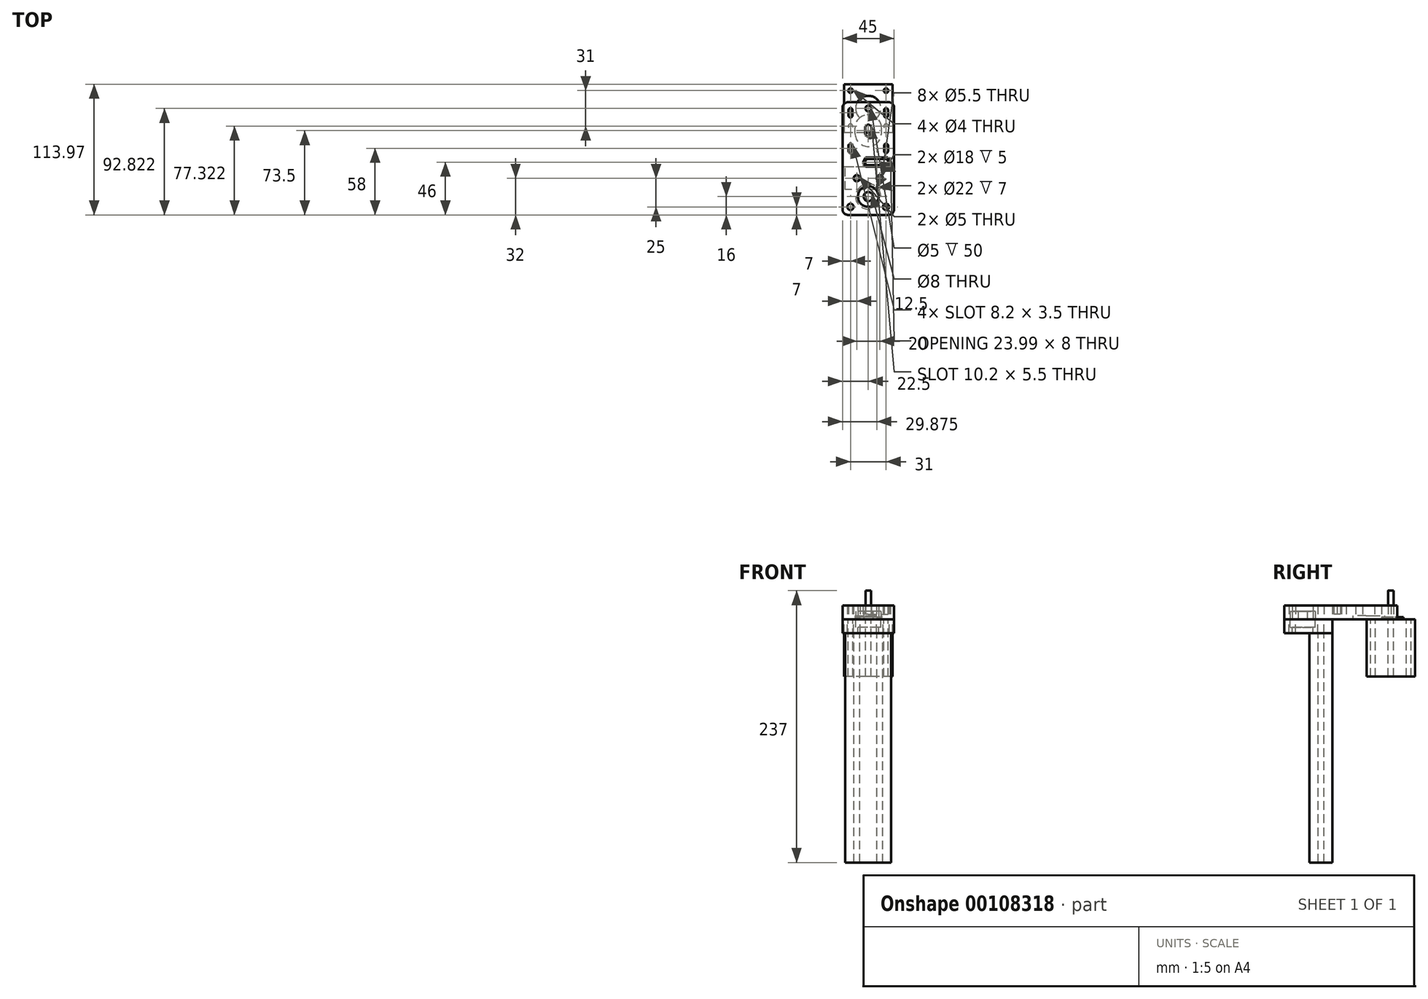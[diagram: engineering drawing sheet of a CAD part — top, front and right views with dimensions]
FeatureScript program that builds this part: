
annotation { "Feature Type Name" : "Feature", "Feature Type Description" : "" }
export const myFeature = defineFeature(function(context is Context, id is Id, definition is map)
    precondition{}
    {
        {
            var Q0;
            Q0=qCreatedBy(makeId("Top.planeOp"),FACE);
            var sketch = newSketch(context, id + "F0", { "sketchPlane" : qUnion([Q0])});
            skCircle(sketch, "E0", {"center": v(0, 76.82) * mm, "radius": 11 * mm});
            skLineSegment(sketch, "E1.bottom", {"start": v(21.15, 97.97) * mm, "end": v(-21.15, 97.97) * mm});
            skLineSegment(sketch, "E1.top", {"start": v(21.15, 55.67) * mm, "end": v(-21.15, 55.67) * mm});
            skLineSegment(sketch, "E1.left", {"start": v(21.15, 97.97) * mm, "end": v(21.15, 55.67) * mm});
            skLineSegment(sketch, "E1.right", {"start": v(-21.15, 97.97) * mm, "end": v(-21.15, 55.67) * mm});
            skLineSegment(sketch, "E2.bottom", {"start": v(15.5, 92.32) * mm, "end": v(-15.5, 92.32) * mm, "construction": true});
            skLineSegment(sketch, "E2.top", {"start": v(15.5, 61.32) * mm, "end": v(-15.5, 61.32) * mm, "construction": true});
            skLineSegment(sketch, "E2.left", {"start": v(15.5, 92.32) * mm, "end": v(15.5, 61.32) * mm, "construction": true});
            skLineSegment(sketch, "E2.right", {"start": v(-15.5, 92.32) * mm, "end": v(-15.5, 61.32) * mm, "construction": true});
            skCircle(sketch, "E3", {"center": v(-15.5, 92.32) * mm, "radius": 2 * mm});
            skCircle(sketch, "E4", {"center": v(15.5, 92.32) * mm, "radius": 2 * mm});
            skCircle(sketch, "E5", {"center": v(15.5, 61.32) * mm, "radius": 2 * mm});
            skCircle(sketch, "E6", {"center": v(-15.5, 61.32) * mm, "radius": 2 * mm});
            skCircle(sketch, "E7", {"center": v(0, 76.82) * mm, "radius": 2.5 * mm});
            skSolve(sketch);
        }
        {
            var Q0;
            Q0=qCreatedBy(makeId("Top.planeOp"),FACE);
            var sketch = newSketch(context, id + "F1", { "sketchPlane" : qUnion([Q0])});
            skCircle(sketch, "E8", {"center": v(0, 0) * mm, "radius": 4 * mm});
            skCircle(sketch, "E9", {"center": v(0, 0) * mm, "radius": 11 * mm});
            skSolve(sketch);
        }
        {
            var Q0;
            Q0=makeQuery(id+"F1.imprint","IMPRINT",FACE,{"disambiguationData":[TD([[makeQuery(id+"F1.imprint","IMPRINT",EDGE,{"derivedFrom":sQuery(id+"F1.wireOp",EDGE,"E8")}),-1.0]])]});
            extrude(context, id + "F2", {"entities" : qUnion([Q0]), "depth" : 7 * mm});
        }
        {
            var Q0;
            Q0=makeQuery(id+"F0.imprint","IMPRINT",FACE,{"disambiguationData":[TD([[makeQuery(id+"F0.imprint","IMPRINT",EDGE,{"derivedFrom":sQuery(id+"F0.wireOp",EDGE,"E0")}),-1.0]])]});
            var Q1;
            Q1=makeQuery(id+"F0.imprint","IMPRINT",FACE,{"disambiguationData":[TD([[makeQuery(id+"F0.imprint","IMPRINT",EDGE,{"derivedFrom":sQuery(id+"F0.wireOp",EDGE,"E0")}),1.0]])]});
            extrude(context, id + "F3", {"entities" : qUnion([Q0, Q1]), "oppositeDirection" : true, "depth" : 50 * mm});
        }
        {
            var Q0;
            Q0=makeQuery(id+"F0.imprint","IMPRINT",FACE,{"disambiguationData":[TD([[makeQuery(id+"F0.imprint","IMPRINT",EDGE,{"derivedFrom":sQuery(id+"F0.wireOp",EDGE,"E0")}),1.0]])]});
            extrude(context, id + "F4", {"entities" : qUnion([Q0]), "operationType" : NewBodyOperationType.ADD, "depth" : 2 * mm});
        }
        {
            var Q0;
            Q0=makeQuery(id+"F0.imprint","IMPRINT",FACE,{"disambiguationData":[TD([[makeQuery(id+"F0.imprint","IMPRINT",EDGE,{"derivedFrom":sQuery(id+"F0.wireOp",EDGE,"E7")}),1.0]])]});
            extrude(context, id + "F5", {"entities" : qUnion([Q0]), "operationType" : NewBodyOperationType.ADD, "depth" : 25 * mm});
        }
        {
            var Q0;
            Q0=qCreatedBy(makeId("Top.planeOp"),FACE);
            var sketch = newSketch(context, id + "F6", { "sketchPlane" : qUnion([Q0])});
            skCircle(sketch, "E10", {"center": v(0, 0) * mm, "radius": 11 * mm});
            skCircle(sketch, "E11", {"center": v(0, 0) * mm, "radius": 9 * mm});
            skLineSegment(sketch, "E12", {"start": v(0, -16) * mm, "end": v(17.5, -16) * mm});
            skLineSegment(sketch, "E13", {"start": v(22.5, -11) * mm, "end": v(22.5, 77.35) * mm});
            skLineSegment(sketch, "E14", {"start": v(17.5, 82.35) * mm, "end": v(-17.5, 82.35) * mm});
            skLineSegment(sketch, "E15", {"start": v(-22.5, 77.35) * mm, "end": v(-22.5, -11) * mm});
            skLineSegment(sketch, "E16", {"start": v(-17.5, -16) * mm, "end": v(0, -16) * mm});
            skLineSegment(sketch, "E17", {"start": v(0, 0) * mm, "end": v(22.5, 0) * mm, "construction": true});
            skCircle(sketch, "E18", {"center": v(-10, 16) * mm, "radius": 2.75 * mm});
            skCircle(sketch, "E19", {"center": v(10, 16) * mm, "radius": 2.75 * mm});
            skLineSegment(sketch, "E20", {"start": v(-10, 16) * mm, "end": v(0, 16) * mm, "construction": true});
            skLineSegment(sketch, "E21", {"start": v(0, 16) * mm, "end": v(10, 16) * mm, "construction": true});
            skArc(sketch, "E22", {"start": v(-11.5, 55.15) * mm, "mid": v(0, 43.65) * mm, "end": v(11.5, 55.15) * mm});
            skLineSegment(sketch, "E23", {"start": v(-11.5, 55.15) * mm, "end": v(-11.5, 59.85) * mm});
            skLineSegment(sketch, "E24", {"start": v(11.5, 55.15) * mm, "end": v(11.5, 59.85) * mm});
            skArc(sketch, "E25", {"start": v(-11.5, 59.85) * mm, "mid": v(0, 71.35) * mm, "end": v(11.5, 59.85) * mm});
            skLineSegment(sketch, "E26.bottom", {"start": v(15.5, 75.35) * mm, "end": v(-15.5, 75.35) * mm, "construction": true});
            skLineSegment(sketch, "E26.top", {"start": v(15.5, 44.35) * mm, "end": v(-15.5, 44.35) * mm, "construction": true});
            skLineSegment(sketch, "E26.left", {"start": v(15.5, 75.35) * mm, "end": v(15.5, 44.35) * mm, "construction": true});
            skLineSegment(sketch, "E26.right", {"start": v(-15.5, 75.35) * mm, "end": v(-15.5, 44.35) * mm, "construction": true});
            skLineSegment(sketch, "E27.bottom", {"start": v(15.5, 70.65) * mm, "end": v(-15.5, 70.65) * mm, "construction": true});
            skLineSegment(sketch, "E27.top", {"start": v(15.5, 39.65) * mm, "end": v(-15.5, 39.65) * mm, "construction": true});
            skLineSegment(sketch, "E27.left", {"start": v(15.5, 70.65) * mm, "end": v(15.5, 39.65) * mm, "construction": true});
            skLineSegment(sketch, "E27.right", {"start": v(-15.5, 70.65) * mm, "end": v(-15.5, 39.65) * mm, "construction": true});
            skArc(sketch, "E28", {"start": v(-17.25, 75.35) * mm, "mid": v(-15.5, 77.1) * mm, "end": v(-13.75, 75.35) * mm});
            skArc(sketch, "E29", {"start": v(13.75, 75.35) * mm, "mid": v(15.5, 77.1) * mm, "end": v(17.25, 75.35) * mm});
            skArc(sketch, "E30", {"start": v(-17.25, 70.65) * mm, "mid": v(-15.5, 68.9) * mm, "end": v(-13.75, 70.65) * mm});
            skArc(sketch, "E31", {"start": v(13.75, 70.65) * mm, "mid": v(15.5, 68.9) * mm, "end": v(17.25, 70.65) * mm});
            skLineSegment(sketch, "E32", {"start": v(-17.25, 70.65) * mm, "end": v(-17.25, 75.35) * mm});
            skLineSegment(sketch, "E33", {"start": v(-13.75, 70.65) * mm, "end": v(-13.75, 75.35) * mm});
            skLineSegment(sketch, "E34", {"start": v(13.75, 70.65) * mm, "end": v(13.75, 75.35) * mm});
            skLineSegment(sketch, "E35", {"start": v(17.25, 70.65) * mm, "end": v(17.25, 75.35) * mm});
            skArc(sketch, "E36", {"start": v(-17.25, 44.35) * mm, "mid": v(-15.5, 46.1) * mm, "end": v(-13.75, 44.35) * mm});
            skArc(sketch, "E37", {"start": v(13.75, 44.35) * mm, "mid": v(15.5, 46.1) * mm, "end": v(17.25, 44.35) * mm});
            skArc(sketch, "E38", {"start": v(-17.25, 39.65) * mm, "mid": v(-15.5, 37.9) * mm, "end": v(-13.75, 39.65) * mm});
            skArc(sketch, "E39", {"start": v(13.75, 39.65) * mm, "mid": v(15.5, 37.9) * mm, "end": v(17.25, 39.65) * mm});
            skLineSegment(sketch, "E40", {"start": v(-17.25, 39.65) * mm, "end": v(-17.25, 44.35) * mm});
            skLineSegment(sketch, "E41", {"start": v(-13.75, 39.65) * mm, "end": v(-13.75, 44.35) * mm});
            skLineSegment(sketch, "E42", {"start": v(13.75, 39.65) * mm, "end": v(13.75, 44.35) * mm});
            skLineSegment(sketch, "E43", {"start": v(17.25, 39.65) * mm, "end": v(17.25, 44.35) * mm});
            skArc(sketch, "E44", {"start": v(-2.75, 59.85) * mm, "mid": v(0, 62.6) * mm, "end": v(2.75, 59.85) * mm});
            skArc(sketch, "E45", {"start": v(-2.75, 55.15) * mm, "mid": v(0, 52.4) * mm, "end": v(2.75, 55.15) * mm});
            skLineSegment(sketch, "E46", {"start": v(-2.75, 55.15) * mm, "end": v(-2.75, 59.85) * mm});
            skLineSegment(sketch, "E47", {"start": v(2.75, 59.85) * mm, "end": v(2.75, 55.15) * mm});
            skLineSegment(sketch, "E48", {"start": v(0, 59.85) * mm, "end": v(22.5, 59.85) * mm, "construction": true});
            skLineSegment(sketch, "E49", {"start": v(0, 59.85) * mm, "end": v(0, 82.35) * mm, "construction": true});
            skPoint(sketch, "E50.visualSharp", {"position": v(-22.5, 82.35) * mm});
            skArc(sketch, "E50.filletArc", {"start": v(-17.5, 82.35) * mm, "mid": v(-21.04, 80.89) * mm, "end": v(-22.5, 77.35) * mm});
            skPoint(sketch, "E51.visualSharp", {"position": v(22.5, 82.35) * mm});
            skArc(sketch, "E51.filletArc", {"start": v(22.5, 77.35) * mm, "mid": v(21.04, 80.89) * mm, "end": v(17.5, 82.35) * mm});
            skPoint(sketch, "E52.visualSharp", {"position": v(22.5, -16) * mm});
            skArc(sketch, "E52.filletArc", {"start": v(17.5, -16) * mm, "mid": v(21.04, -14.54) * mm, "end": v(22.5, -11) * mm});
            skPoint(sketch, "E53.visualSharp", {"position": v(-22.5, -16) * mm});
            skArc(sketch, "E53.filletArc", {"start": v(-22.5, -11) * mm, "mid": v(-21.04, -14.54) * mm, "end": v(-17.5, -16) * mm});
            skLineSegment(sketch, "E54.bottom", {"start": v(20, 26) * mm, "end": v(-20, 26) * mm, "construction": true});
            skLineSegment(sketch, "E54.top", {"start": v(20, 6) * mm, "end": v(-20, 6) * mm, "construction": true});
            skLineSegment(sketch, "E54.left", {"start": v(20, 26) * mm, "end": v(20, 6) * mm, "construction": true});
            skLineSegment(sketch, "E54.right", {"start": v(-20, 26) * mm, "end": v(-20, 6) * mm, "construction": true});
            skPoint(sketch, "E54.middle", {"position": v(0, 16) * mm});
            skCircle(sketch, "E55", {"center": v(0, 0) * mm, "radius": 4 * mm});
            skLineSegment(sketch, "E56", {"start": v(-21.15, 34) * mm, "end": v(21.15, 34) * mm, "construction": true});
            skLineSegment(sketch, "E57", {"start": v(21.15, 34) * mm, "end": v(21.15, 81) * mm, "construction": true});
            skLineSegment(sketch, "E58", {"start": v(21.15, 81) * mm, "end": v(-21.15, 81) * mm, "construction": true});
            skLineSegment(sketch, "E59", {"start": v(-21.15, 81) * mm, "end": v(-21.15, 34) * mm, "construction": true});
            skPoint(sketch, "E60", {"position": v(0, 34) * mm});
            skLineSegment(sketch, "E61", {"start": v(15.5, 39.65) * mm, "end": v(21.15, 39.65) * mm, "construction": true});
            skLineSegment(sketch, "E62", {"start": v(15.5, 39.65) * mm, "end": v(15.5, 34) * mm, "construction": true});
            skLineSegment(sketch, "E63", {"start": v(15.5, 75.35) * mm, "end": v(15.5, 81) * mm, "construction": true});
            skLineSegment(sketch, "E64", {"start": v(-22.5, 26) * mm, "end": v(22.5, 26) * mm});
            skCircle(sketch, "E65", {"center": v(15.5, -9) * mm, "radius": 2.75 * mm});
            skCircle(sketch, "E66", {"center": v(-15.5, -9) * mm, "radius": 2.75 * mm});
            skLineSegment(sketch, "E67", {"start": v(22.5, -9) * mm, "end": v(15.5, -9) * mm, "construction": true});
            skLineSegment(sketch, "E68", {"start": v(-15.5, -9) * mm, "end": v(-22.5, -9) * mm, "construction": true});
            skCircle(sketch, "E69", {"center": v(0, 0) * mm, "radius": 10.2 * mm, "construction": true});
            skArc(sketch, "E70", {"start": v(0, 27.25) * mm, "mid": v(-2.75, 30) * mm, "end": v(0, 32.75) * mm});
            skArc(sketch, "E71", {"start": v(14.75, 32.75) * mm, "mid": v(17.5, 30) * mm, "end": v(14.75, 27.25) * mm});
            skLineSegment(sketch, "E72", {"start": v(0, 32.75) * mm, "end": v(14.75, 32.75) * mm});
            skLineSegment(sketch, "E73", {"start": v(14.75, 27.25) * mm, "end": v(0, 27.25) * mm});
            skLineSegment(sketch, "E74", {"start": v(0, 34) * mm, "end": v(0, 26) * mm, "construction": true});
            skCircle(sketch, "E75", {"center": v(0, 0) * mm, "radius": 12.75 * mm, "construction": true});
            skCircle(sketch, "E76", {"center": v(0, 55.15) * mm, "radius": 12.75 * mm, "construction": true});
            skLineSegment(sketch, "E77", {"start": v(12.75, 55.15) * mm, "end": v(12.75, 0) * mm, "construction": true});
            skLineSegment(sketch, "E78", {"start": v(-12.75, 55.15) * mm, "end": v(-12.75, 0) * mm, "construction": true});
            skCircle(sketch, "E79", {"center": v(0, 30) * mm, "radius": 6.35 * mm, "construction": true});
            skCircle(sketch, "E80", {"center": v(14.75, 30) * mm, "radius": 6.35 * mm, "construction": true});
            skLineSegment(sketch, "E81", {"start": v(15.5, -9) * mm, "end": v(15.5, -16) * mm, "construction": true});
            skLineSegment(sketch, "E82", {"start": v(-4.62, 30) * mm, "end": v(-2.3, 26) * mm});
            skLineSegment(sketch, "E83", {"start": v(-4.62, 30) * mm, "end": v(-2.3, 34) * mm});
            skLineSegment(sketch, "E84", {"start": v(-2.3, 34) * mm, "end": v(17.06, 34) * mm});
            skLineSegment(sketch, "E85", {"start": v(17.06, 34) * mm, "end": v(19.37, 30) * mm});
            skLineSegment(sketch, "E86", {"start": v(19.37, 30) * mm, "end": v(17.06, 26) * mm});
            skLineSegment(sketch, "E87", {"start": v(18.21, 28) * mm, "end": v(14.75, 30) * mm, "construction": true});
            skLineSegment(sketch, "E88", {"start": v(18.21, 32) * mm, "end": v(14.75, 30) * mm, "construction": true});
            skLineSegment(sketch, "E89", {"start": v(-3.46, 32) * mm, "end": v(0, 30) * mm, "construction": true});
            skLineSegment(sketch, "E90", {"start": v(-3.46, 28) * mm, "end": v(0, 30) * mm, "construction": true});
            skPoint(sketch, "E91", {"position": v(17.5, 30) * mm});
            skLineSegment(sketch, "E92", {"start": v(14.75, 30) * mm, "end": v(14.75, 34) * mm, "construction": true});
            skSolve(sketch);
        }
        {
            var Q0;
            Q0=makeQuery(id+"F6.imprint","IMPRINT",FACE,{"disambiguationData":[TD([[makeQuery(id+"F6.imprint","IMPRINT",EDGE,{"derivedFrom":sQuery(id+"F6.wireOp",EDGE,"E10")}),-1.0]])]});
            var Q1;
            Q1=makeQuery(id+"F6.imprint","IMPRINT",FACE,{"disambiguationData":[TD([[makeQuery(id+"F6.imprint","IMPRINT",EDGE,{"derivedFrom":sQuery(id+"F6.wireOp",EDGE,"E22")}),1.0]])]});
            var Q2;
            Q2=makeQuery(id+"F6.imprint","IMPRINT",FACE,{"disambiguationData":[TD([[makeQuery(id+"F6.imprint","IMPRINT",EDGE,{"derivedFrom":sQuery(id+"F6.wireOp",EDGE,"E10")}),1.0]])]});
            var Q3;
            Q3=makeQuery(id+"F6.imprint","IMPRINT",FACE,{"disambiguationData":[TD([[makeQuery(id+"F6.imprint","IMPRINT",EDGE,{"derivedFrom":sQuery(id+"F6.wireOp",EDGE,"E14")}),1.0]])]});
            var Q4;
            Q4=makeQuery(id+"F6.imprint","IMPRINT",FACE,{"disambiguationData":[TD([[makeQuery(id+"F6.imprint","IMPRINT",EDGE,{"derivedFrom":sQuery(id+"F6.wireOp",EDGE,"E70")}),1.0]])]});
            extrude(context, id + "F7", {"entities" : qUnion([Q0, Q1, Q2, Q3, Q4]), "depth" : 12 * mm});
        }
        {
            var Q0;
            Q0=makeQuery(id+"F6.imprint","IMPRINT",FACE,{"disambiguationData":[TD([[makeQuery(id+"F6.imprint","IMPRINT",EDGE,{"derivedFrom":sQuery(id+"F6.wireOp",EDGE,"E10")}),1.0]])]});
            extrude(context, id + "F8", {"entities" : qUnion([Q0]), "operationType" : NewBodyOperationType.REMOVE, "depth" : 7 * mm});
        }
        {
            var Q0;
            Q0=makeQuery(id+"F6.imprint","IMPRINT",FACE,{"disambiguationData":[TD([[makeQuery(id+"F6.imprint","IMPRINT",EDGE,{"derivedFrom":sQuery(id+"F6.wireOp",EDGE,"E22")}),1.0]])]});
            extrude(context, id + "F9", {"entities" : qUnion([Q0]), "operationType" : NewBodyOperationType.REMOVE, "depth" : 3 * mm});
        }
        {
            var Q0;
            Q0=makeQuery(id+"F6.imprint","IMPRINT",FACE,{"disambiguationData":[TD([[makeQuery(id+"F6.imprint","IMPRINT",EDGE,{"derivedFrom":sQuery(id+"F6.wireOp",EDGE,"E10")}),-1.0]])]});
            var Q1;
            Q1=makeQuery(id+"F6.imprint","IMPRINT",FACE,{"disambiguationData":[TD([[makeQuery(id+"F6.imprint","IMPRINT",EDGE,{"derivedFrom":sQuery(id+"F6.wireOp",EDGE,"E10")}),1.0]])]});
            extrude(context, id + "F10", {"entities" : qUnion([Q0, Q1]), "oppositeDirection" : true, "depth" : 12 * mm});
        }
        {
            var Q0;
            Q0=makeQuery(id+"F6.imprint","IMPRINT",FACE,{"disambiguationData":[TD([[makeQuery(id+"F6.imprint","IMPRINT",EDGE,{"derivedFrom":sQuery(id+"F6.wireOp",EDGE,"E10")}),1.0]])]});
            extrude(context, id + "F11", {"entities" : qUnion([Q0]), "operationType" : NewBodyOperationType.REMOVE, "oppositeDirection" : true, "depth" : 7 * mm});
        }
        {
            var Q0;
            Q0=makeQuery(id+"F10.opExtrude","CAP_FACE",FACE,{"disambiguationData":[OSD([sQuery(id+"F6.wireOp",EDGE,"E11"),sQuery(id+"F6.wireOp",EDGE,"E12"),sQuery(id+"F6.wireOp",EDGE,"E13"),sQuery(id+"F6.wireOp",EDGE,"E15"),sQuery(id+"F6.wireOp",EDGE,"E16"),sQuery(id+"F6.wireOp",EDGE,"E18"),sQuery(id+"F6.wireOp",EDGE,"E19"),sQuery(id+"F6.wireOp",EDGE,"E52.filletArc"),sQuery(id+"F6.wireOp",EDGE,"E53.filletArc"),sQuery(id+"F6.wireOp",EDGE,"E64")])],"isStart":false});
            var sketch = newSketch(context, id + "F12", { "sketchPlane" : qUnion([Q0])});
            skLineSegment(sketch, "E93.bottom", {"start": v(20, -6) * mm, "end": v(-20, -6) * mm});
            skLineSegment(sketch, "E93.top", {"start": v(20, -26) * mm, "end": v(-20, -26) * mm});
            skLineSegment(sketch, "E93.left", {"start": v(20, -6) * mm, "end": v(20, -26) * mm});
            skLineSegment(sketch, "E93.right", {"start": v(-20, -6) * mm, "end": v(-20, -26) * mm});
            skPoint(sketch, "E93.middle", {"position": v(0, -16) * mm});
            skLineSegment(sketch, "E94", {"start": v(-20, -16) * mm, "end": v(0, -16) * mm, "construction": true});
            skLineSegment(sketch, "E95", {"start": v(20, -16) * mm, "end": v(0, -16) * mm, "construction": true});
            skCircle(sketch, "E96", {"center": v(-10, -16) * mm, "radius": 2.5 * mm});
            skCircle(sketch, "E97", {"center": v(10, -16) * mm, "radius": 2.5 * mm});
            skSolve(sketch);
        }
        {
            var Q0;
            Q0 = qSketchRegion(id + "F12", true);
            extrude(context, id + "F13", {"entities" : qUnion([Q0]), "depth" : 200 * mm});
        }
        {
            var Q0;
            Q0=makeQuery(id+"F6.imprint","IMPRINT",FACE,{"disambiguationData":[TD([[makeQuery(id+"F6.imprint","IMPRINT",EDGE,{"derivedFrom":sQuery(id+"F6.wireOp",EDGE,"E70")}),1.0]])]});
            extrude(context, id + "F14", {"entities" : qUnion([Q0]), "operationType" : NewBodyOperationType.REMOVE, "depth" : 4.5 * mm});
        }
    });
